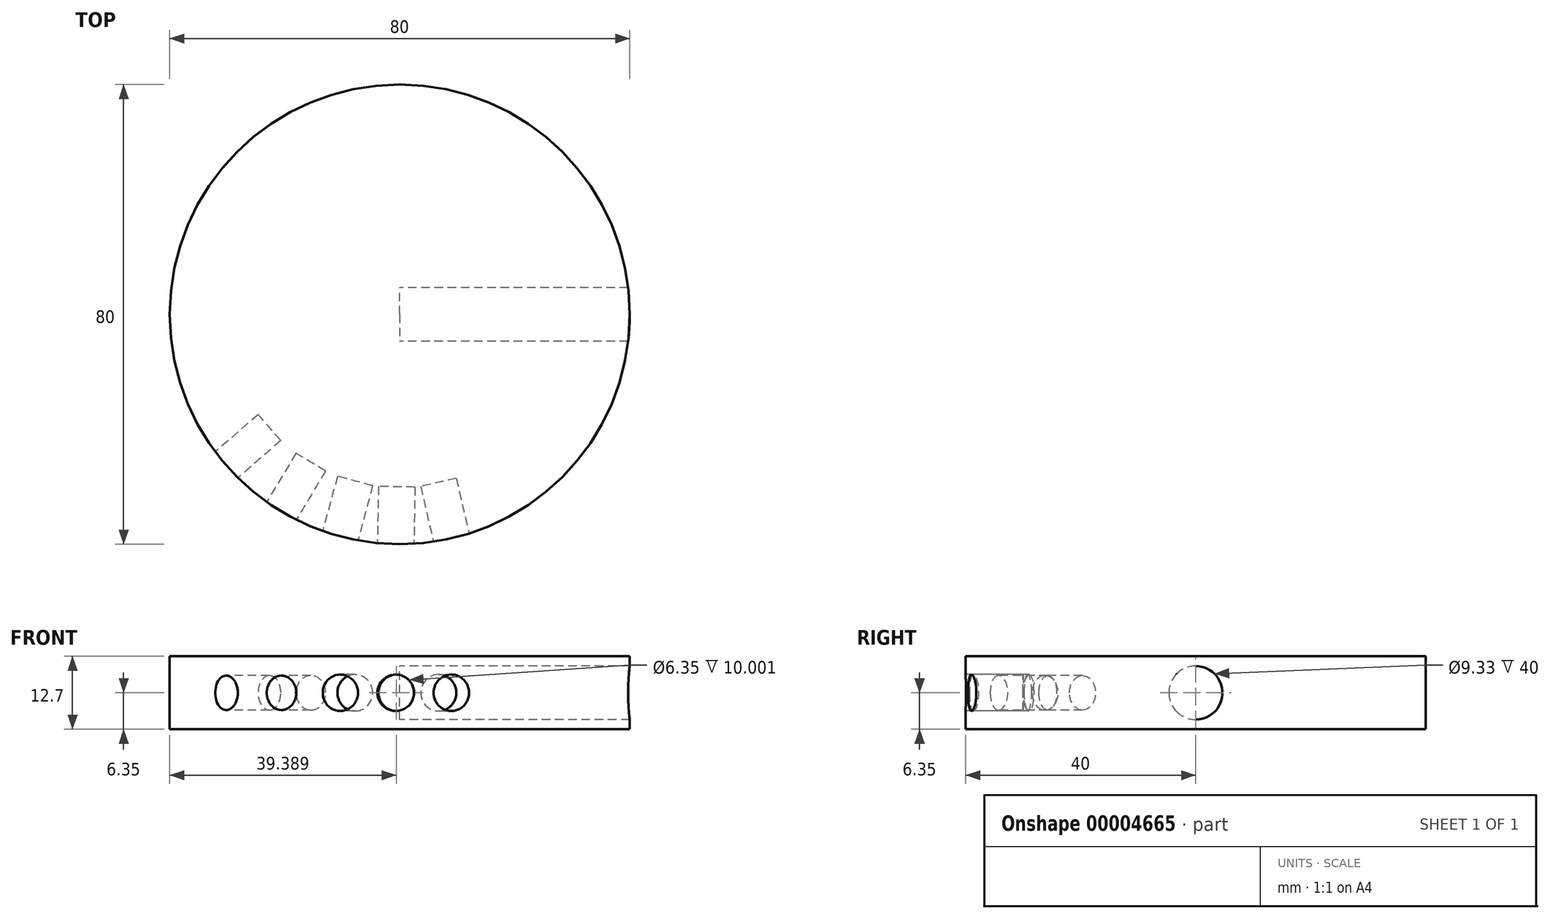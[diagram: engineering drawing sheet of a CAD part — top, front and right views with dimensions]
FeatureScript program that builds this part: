
annotation { "Feature Type Name" : "Feature", "Feature Type Description" : "" }
export const myFeature = defineFeature(function(context is Context, id is Id, definition is map)
    precondition{}
    {
        {
            var Q0;
            Q0=qCreatedBy(makeId("Top.planeOp"),FACE);
            var sketch = newSketch(context, id + "F0", { "sketchPlane" : qUnion([Q0])});
            skCircle(sketch, "E0", {"center": v(0, 0) * mm, "radius": 40 * mm});
            skLineSegment(sketch, "E1", {"start": v(0, 0) * mm, "end": v(-10.35, -38.64) * mm, "construction": true});
            skLineSegment(sketch, "E2", {"start": v(0, 0) * mm, "end": v(-20.6, -34.29) * mm, "construction": true});
            skLineSegment(sketch, "E3", {"start": v(0, 0) * mm, "end": v(-30.19, -26.24) * mm, "construction": true});
            skSolve(sketch);
        }
        {
            var Q0;
            Q0 = qSketchRegion(id + "F0", true);
            extrude(context, id + "F1", {"entities" : qUnion([Q0]), "endBound" : BoundingType.SYMMETRIC, "depth" : 12.7 * mm});
        }
        {
            var Q0;
            Q0=qCreatedBy(makeId("Front.planeOp"),FACE);
            var sketch = newSketch(context, id + "F2", { "sketchPlane" : qUnion([Q0])});
            skLineSegment(sketch, "E4", {"start": v(0, 0) * mm, "end": v(0, 57) * mm, "construction": true});
            skSolve(sketch);
        }
        {
            var Q0;
            Q0=sQuery(id+"F0.wireOp",VERTEX,"E1.end");
            var Q1;
            Q1=sQuery(id+"F0.wireOp",EDGE,"E1");
            cPlane(context, id + "F3", {"entities" : qUnion([Q0, Q1]), "cplaneType" : CPlaneType.LINE_POINT, "offset" : 150 * mm, "width" : 150 * mm, "height" : 150 * mm});
        }
        {
            var Q0;
            Q0=sQuery(id+"F0.wireOp",VERTEX,"E2.end");
            var Q1;
            Q1=sQuery(id+"F0.wireOp",EDGE,"E2");
            cPlane(context, id + "F4", {"entities" : qUnion([Q0, Q1]), "cplaneType" : CPlaneType.LINE_POINT, "offset" : 150 * mm, "width" : 150 * mm, "height" : 150 * mm});
        }
        {
            var Q0;
            Q0=sQuery(id+"F0.wireOp",VERTEX,"E3.end");
            var Q1;
            Q1=sQuery(id+"F0.wireOp",EDGE,"E3");
            cPlane(context, id + "F5", {"entities" : qUnion([Q0, Q1]), "cplaneType" : CPlaneType.LINE_POINT, "offset" : 150 * mm, "width" : 150 * mm, "height" : 150 * mm});
        }
        {
            var Q0;
            Q0=qCreatedBy(id+"F3.planeOp",FACE);
            var sketch = newSketch(context, id + "F6", { "sketchPlane" : qUnion([Q0])});
            skCircle(sketch, "E5", {"center": v(0, 0) * mm, "radius": 3.17 * mm});
            skSolve(sketch);
        }
        {
            var Q0;
            Q0 = qSketchRegion(id + "F6", true);
            extrude(context, id + "F7", {"entities" : qUnion([Q0]), "operationType" : NewBodyOperationType.REMOVE, "oppositeDirection" : true, "depth" : 10 * mm});
        }
        {
            var Q0;
            Q0=qCreatedBy(id+"F4.planeOp",FACE);
            var sketch = newSketch(context, id + "F8", { "sketchPlane" : qUnion([Q0])});
            skCircle(sketch, "E6", {"center": v(0, 0) * mm, "radius": 3 * mm});
            skSolve(sketch);
        }
        {
            var Q0;
            Q0 = qSketchRegion(id + "F8", true);
            extrude(context, id + "F9", {"entities" : qUnion([Q0]), "operationType" : NewBodyOperationType.REMOVE, "oppositeDirection" : true, "depth" : 10 * mm});
        }
        {
            var Q0;
            Q0=qCreatedBy(id+"F5.planeOp",FACE);
            var sketch = newSketch(context, id + "F10", { "sketchPlane" : qUnion([Q0])});
            skCircle(sketch, "E7", {"center": v(0, 0) * mm, "radius": 3 * mm});
            skSolve(sketch);
        }
        {
            var Q0;
            Q0 = qSketchRegion(id + "F10", true);
            extrude(context, id + "F11", {"entities" : qUnion([Q0]), "operationType" : NewBodyOperationType.REMOVE, "oppositeDirection" : true, "depth" : 10 * mm});
        }
        {
            var Q0;
            Q0=makeQuery(id+"F7.boolean.opBoolean","COPY",FACE,{"derivedFrom":makeQuery(id+"F7.opExtrude","SWEPT_FACE",FACE,{"disambiguationData":[OSD([sQuery(id+"F6.wireOp",EDGE,"E5")])]})});
            var Q1;
            Q1=makeQuery(id+"F7.boolean.opBoolean","COPY",FACE,{"derivedFrom":makeQuery(id+"F7.opExtrude","CAP_FACE",FACE,{"disambiguationData":[OSD([sQuery(id+"F6.wireOp",EDGE,"E5")])],"isStart":false})});
            var Q2;
            Q2=sQuery(id+"F2.wireOp",EDGE,"E4");
            circularPattern(context, id + "F12", {"faces" : qUnion([Q0, Q1]), "axis" : qUnion([Q2]), "angle" : 14 * degree, "instanceCount" : 3, "patternType" : PatternType.FACE});
        }
        {
            var Q0;
            Q0=qCreatedBy(makeId("Right.planeOp"),FACE);
            var sketch = newSketch(context, id + "F13", { "sketchPlane" : qUnion([Q0])});
            skCircle(sketch, "E8", {"center": v(0, 0) * mm, "radius": 4.66 * mm});
            skSolve(sketch);
        }
        {
            var Q0;
            Q0 = qSketchRegion(id + "F13", true);
            extrude(context, id + "F14", {"entities" : qUnion([Q0]), "depth" : 62.04 * mm});
        }
        {
            var Q0;
            Q0=makeQuery(id+"F14.opExtrude","SWEPT_BODY",BODY,{"disambiguationData":[OSD([sQuery(id+"F13.wireOp",EDGE,"E8")])]});
            var Q1;
            Q1=makeQuery(id+"F1.opExtrude","SWEPT_BODY",BODY,{"disambiguationData":[OSD([sQuery(id+"F0.wireOp",EDGE,"E0")])]});
            booleanBodies(context, id + "F15", {"operationType" : BooleanOperationType.SUBTRACTION, "tools" : qUnion([Q0]), "targets" : qUnion([Q1])});
        }
    });
